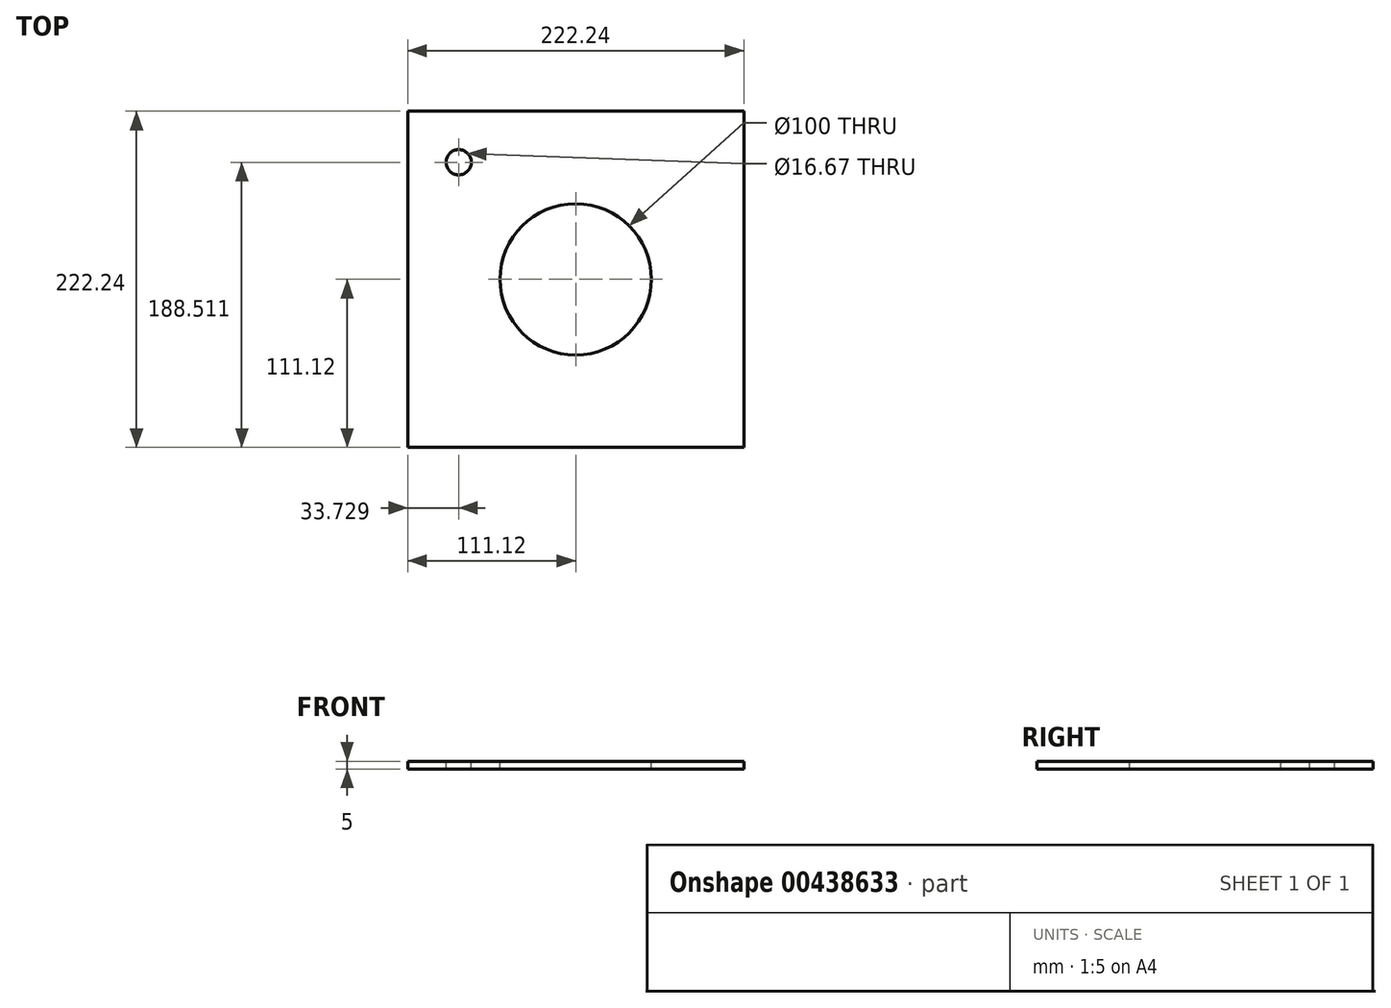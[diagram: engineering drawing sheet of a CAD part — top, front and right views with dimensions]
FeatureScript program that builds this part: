
annotation { "Feature Type Name" : "Feature", "Feature Type Description" : "" }
export const myFeature = defineFeature(function(context is Context, id is Id, definition is map)
    precondition{}
    {
        {
            var Q0;
            Q0=qCreatedBy(makeId("Top.planeOp"),FACE);
            var sketch = newSketch(context, id + "F0", { "sketchPlane" : qUnion([Q0])});
            skLineSegment(sketch, "E0.bottom", {"start": v(111.12, 111.13) * mm, "end": v(-111.13, 111.13) * mm});
            skLineSegment(sketch, "E0.top", {"start": v(111.13, -111.13) * mm, "end": v(-111.12, -111.13) * mm});
            skLineSegment(sketch, "E0.left", {"start": v(111.12, 111.13) * mm, "end": v(111.13, -111.13) * mm});
            skLineSegment(sketch, "E0.right", {"start": v(-111.13, 111.13) * mm, "end": v(-111.12, -111.13) * mm});
            skPoint(sketch, "E0.middle", {"position": v(0, 0) * mm});
            skSolve(sketch);
        }
        {
            var Q0;
            Q0 = qSketchRegion(id + "F0", true);
            extrude(context, id + "F1", {"entities" : qUnion([Q0]), "depth" : 5 * mm});
        }
        {
            var Q0;
            Q0=makeQuery(id+"F1.opExtrude","CAP_FACE",FACE,{"disambiguationData":[OSD([sQuery(id+"F0.wireOp",EDGE,"E0.bottom"),sQuery(id+"F0.wireOp",EDGE,"E0.top"),sQuery(id+"F0.wireOp",EDGE,"E0.left"),sQuery(id+"F0.wireOp",EDGE,"E0.right")])],"isStart":false});
            var sketch = newSketch(context, id + "F2", { "sketchPlane" : qUnion([Q0])});
            skCircle(sketch, "E1", {"center": v(0, 0) * mm, "radius": 50 * mm});
            skSolve(sketch);
        }
        {
            var Q0;
            Q0 = qSketchRegion(id + "F2", true);
            extrude(context, id + "F3", {"entities" : qUnion([Q0]), "operationType" : NewBodyOperationType.REMOVE, "endBound" : BoundingType.THROUGH_ALL, "oppositeDirection" : true, "depth" : 25 * mm});
        }
        {
            var Q0;
            Q0=makeQuery(id+"F1.opExtrude","CAP_FACE",FACE,{"disambiguationData":[OSD([sQuery(id+"F0.wireOp",EDGE,"E0.bottom"),sQuery(id+"F0.wireOp",EDGE,"E0.top"),sQuery(id+"F0.wireOp",EDGE,"E0.left"),sQuery(id+"F0.wireOp",EDGE,"E0.right")])],"isStart":false});
            var sketch = newSketch(context, id + "F4", { "sketchPlane" : qUnion([Q0])});
            skCircle(sketch, "E2", {"center": v(-77.4, 77.4) * mm, "radius": 8.33 * mm});
            skSolve(sketch);
        }
        {
            var Q0;
            Q0=makeQuery(id+"F4.imprint","IMPRINT",FACE,{"disambiguationData":[TD([[makeQuery(id+"F4.imprint","IMPRINT",EDGE,{"derivedFrom":sQuery(id+"F4.wireOp",EDGE,"E2")}),1.0]])]});
            extrude(context, id + "F5", {"entities" : qUnion([Q0]), "operationType" : NewBodyOperationType.REMOVE, "endBound" : BoundingType.THROUGH_ALL, "oppositeDirection" : true, "depth" : 25 * mm});
        }
    });
